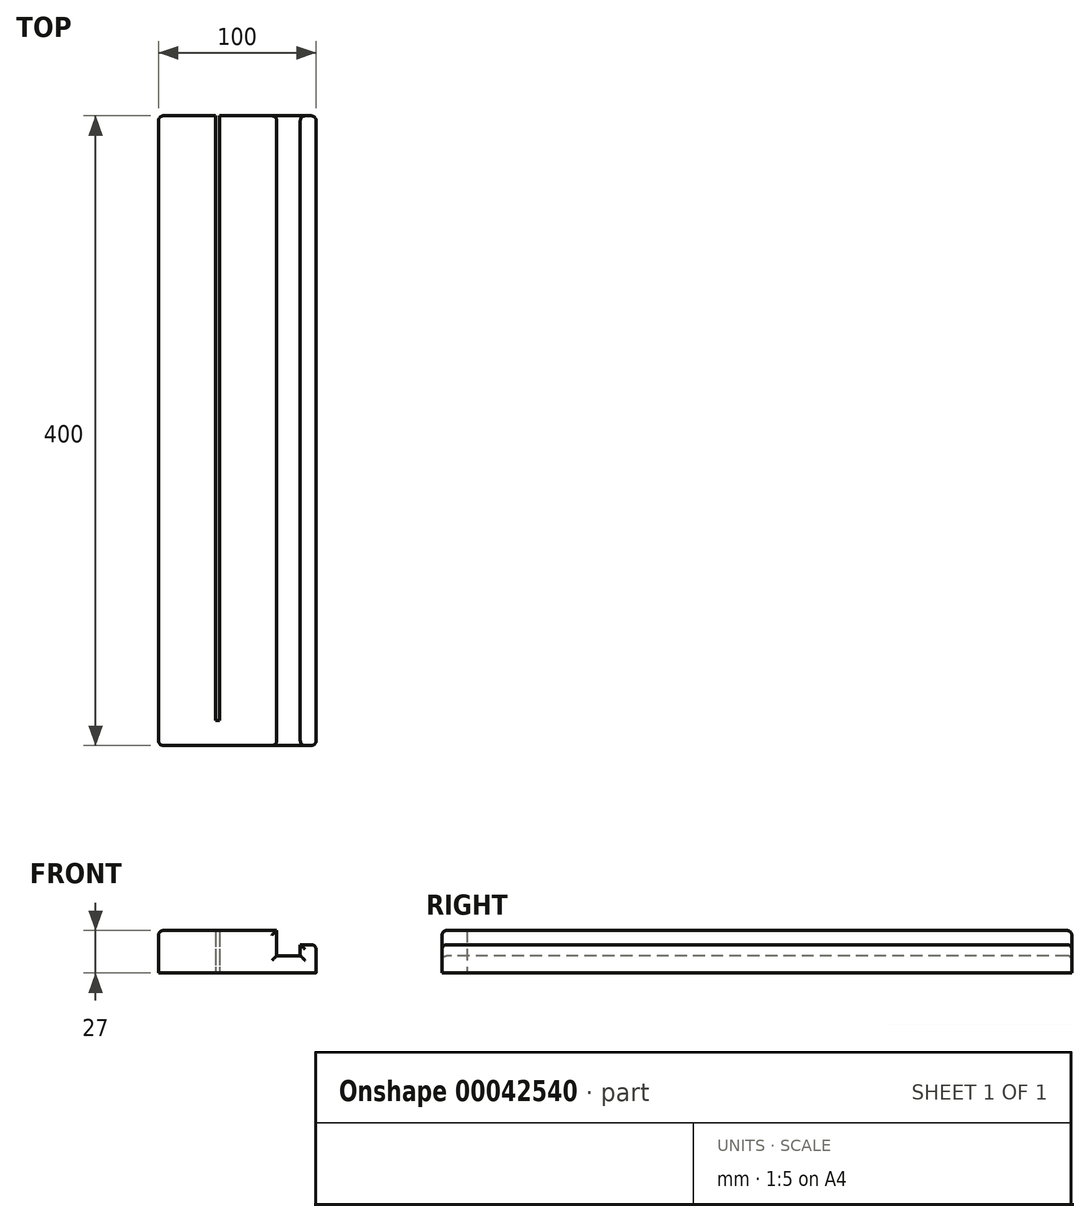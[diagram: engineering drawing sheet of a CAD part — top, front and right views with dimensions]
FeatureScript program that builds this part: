
annotation { "Feature Type Name" : "Feature", "Feature Type Description" : "" }
export const myFeature = defineFeature(function(context is Context, id is Id, definition is map)
    precondition{}
    {
        {
            assignVariable(context, id + "F0", {"name" : "WoodThickness", "anyValue" : 27});
        }
        {
            var Q0;
            Q0=qCreatedBy(makeId("Top.planeOp"),FACE);
            var sketch = newSketch(context, id + "F1", { "sketchPlane" : qUnion([Q0])});
            skLineSegment(sketch, "E0.bottom", {"start": v(-37.5, 200) * mm, "end": v(62.5, 200) * mm});
            skLineSegment(sketch, "E0.top", {"start": v(-37.5, -200) * mm, "end": v(62.5, -200) * mm});
            skLineSegment(sketch, "E0.left", {"start": v(-37.5, 200) * mm, "end": v(-37.5, -200) * mm});
            skLineSegment(sketch, "E0.right", {"start": v(62.5, 200) * mm, "end": v(62.5, -200) * mm});
            skCircle(sketch, "E1", {"center": v(0, -190) * mm, "radius": 6 * mm});
            skLineSegment(sketch, "E2.top", {"start": v(-1.25, 200) * mm, "end": v(1.25, 200) * mm});
            skLineSegment(sketch, "E2.left", {"start": v(-1.25, -184.13) * mm, "end": v(-1.25, 200) * mm});
            skLineSegment(sketch, "E2.right", {"start": v(1.25, -184.13) * mm, "end": v(1.25, 200) * mm});
            skLineSegment(sketch, "E3", {"start": v(52.5, 200) * mm, "end": v(52.5, -200) * mm});
            skLineSegment(sketch, "E4", {"start": v(37.5, 200) * mm, "end": v(37.5, -200) * mm});
            skSolve(sketch);
        }
        {
            var Q0;
            {var subQ6=sQuery(id+"F1.wireOp",EDGE,"E0.left");Q0=makeQuery(id+"F1.imprint","IMPRINT",FACE,{"disambiguationData":[TD([[makeQuery(id+"F1.imprint","IMPRINT",EDGE,{"derivedFrom":subQ6}),1.0]])]});}
            var Q1;
            Q1=makeQuery(id+"F1.imprint","IMPRINT",FACE,{"disambiguationData":[TD([[makeQuery(id+"F1.imprint","IMPRINT",EDGE,{"derivedFrom":sQuery(id+"F1.wireOp",EDGE,"E2.top")}),-1.0]])]});
            var Q2;
            {var subQ0=sQuery(id+"F1.wireOp",EDGE,"E1");var subQ2=makeQuery(id+"F1.imprint","INTERSECT",VERTEX,{"derivedFrom":[subQ0,sQuery(id+"F1.wireOp",EDGE,"E2.left")]});Q2=makeQuery(id+"F1.imprint","IMPRINT",FACE,{"disambiguationData":[TD([[makeQuery(id+"F1.imprint","IMPRINT",EDGE,{"disambiguationData":[TD([[subQ2,1.0]])],"derivedFrom":subQ0}),1.0]])]});}
            extrude(context, id + "F2", {"entities" : qUnion([Q0, Q1, Q2]), "depth" : (getVariable(context, 'WoodThickness')) * mm});
        }
        {
            var Q0;
            {var subQ1=sQuery(id+"F1.wireOp",EDGE,"E3");Q0=makeQuery(id+"F1.imprint","IMPRINT",FACE,{"disambiguationData":[TD([[makeQuery(id+"F1.imprint","IMPRINT",EDGE,{"derivedFrom":subQ1}),-1.0]])]});}
            extrude(context, id + "F3", {"entities" : qUnion([Q0]), "operationType" : NewBodyOperationType.ADD, "depth" : (getVariable(context, 'WoodThickness') - 16) * mm});
        }
        {
            var Q0;
            {var subQ1=sQuery(id+"F1.wireOp",EDGE,"E0.right");Q0=makeQuery(id+"F1.imprint","IMPRINT",FACE,{"disambiguationData":[TD([[makeQuery(id+"F1.imprint","IMPRINT",EDGE,{"derivedFrom":subQ1}),-1.0]])]});}
            extrude(context, id + "F4", {"entities" : qUnion([Q0]), "operationType" : NewBodyOperationType.ADD, "depth" : (getVariable(context, 'WoodThickness') - 9) * mm});
        }
        {
            var Q0;
            Q0=makeQuery(id+"F2.opExtrude","CAP_EDGE",EDGE,{"disambiguationData":[OSD([sQuery(id+"F1.wireOp",EDGE,"E0.left")])],"isStart":false});
            var Q1;
            Q1=makeQuery(id+"F2.opExtrude","CAP_EDGE",EDGE,{"disambiguationData":[OSD([sQuery(id+"F1.wireOp",EDGE,"E0.top")])],"isStart":false});
            var Q2;
            Q2=makeQuery(id+"F2.opExtrude","CAP_EDGE",EDGE,{"disambiguationData":[OSD([sQuery(id+"F1.wireOp",EDGE,"E0.bottom"),sQuery(id+"F1.wireOp",EDGE,"E2.top")])],"isStart":false});
            var Q3;
            Q3=makeQuery(id+"F4.opExtrude","CAP_EDGE",EDGE,{"disambiguationData":[OSD([sQuery(id+"F1.wireOp",EDGE,"E0.right")])],"isStart":false});
            var Q4;
            Q4=makeQuery(id+"F2.opExtrude","SWEPT_EDGE",EDGE,{"disambiguationData":[OSD([sQuery(id+"F1.wireOp",EDGE,"E0.top"),sQuery(id+"F1.wireOp",EDGE,"E4")])]});
            var Q5;
            Q5=makeQuery(id+"F2.opExtrude","SWEPT_EDGE",EDGE,{"disambiguationData":[OSD([sQuery(id+"F1.wireOp",EDGE,"E0.bottom"),sQuery(id+"F1.wireOp",EDGE,"E4")])]});
            var Q6;
            Q6=makeQuery(id+"F2.opExtrude","SWEPT_EDGE",EDGE,{"disambiguationData":[OSD([sQuery(id+"F1.wireOp",EDGE,"E0.top"),sQuery(id+"F1.wireOp",EDGE,"E0.left")])]});
            var Q7;
            Q7=makeQuery(id+"F4.opExtrude","SWEPT_EDGE",EDGE,{"disambiguationData":[OSD([sQuery(id+"F1.wireOp",EDGE,"E0.top"),sQuery(id+"F1.wireOp",EDGE,"E0.right")])]});
            var Q8;
            Q8=makeQuery(id+"F4.opExtrude","CAP_EDGE",EDGE,{"disambiguationData":[OSD([sQuery(id+"F1.wireOp",EDGE,"E0.top")])],"isStart":false});
            var Q9;
            Q9=makeQuery(id+"F4.opExtrude","SWEPT_EDGE",EDGE,{"disambiguationData":[OSD([sQuery(id+"F1.wireOp",EDGE,"E0.top"),sQuery(id+"F1.wireOp",EDGE,"E3")])]});
            var Q10;
            Q10=makeQuery(id+"F3.opExtrude","CAP_EDGE",EDGE,{"disambiguationData":[OSD([sQuery(id+"F1.wireOp",EDGE,"E0.top")])],"isStart":false});
            var Q11;
            Q11=makeQuery(id+"F3.opExtrude","CAP_EDGE",EDGE,{"disambiguationData":[OSD([sQuery(id+"F1.wireOp",EDGE,"E0.bottom")])],"isStart":false});
            var Q12;
            Q12=makeQuery(id+"F4.opExtrude","CAP_EDGE",EDGE,{"disambiguationData":[OSD([sQuery(id+"F1.wireOp",EDGE,"E0.bottom")])],"isStart":false});
            var Q13;
            Q13=makeQuery(id+"F4.opExtrude","SWEPT_EDGE",EDGE,{"disambiguationData":[OSD([sQuery(id+"F1.wireOp",EDGE,"E0.bottom"),sQuery(id+"F1.wireOp",EDGE,"E0.right")])]});
            var Q14;
            Q14=makeQuery(id+"F4.opExtrude","SWEPT_EDGE",EDGE,{"disambiguationData":[OSD([sQuery(id+"F1.wireOp",EDGE,"E0.bottom"),sQuery(id+"F1.wireOp",EDGE,"E3")])]});
            var Q15;
            Q15=makeQuery(id+"F2.opExtrude","SWEPT_EDGE",EDGE,{"disambiguationData":[OSD([sQuery(id+"F1.wireOp",EDGE,"E0.bottom"),sQuery(id+"F1.wireOp",EDGE,"E0.left")])]});
            fillet(context, id + "F5", {"entities" : qUnion([Q0, Q1, Q2, Q3, Q4, Q5, Q6, Q7, Q8, Q9, Q10, Q11, Q12, Q13, Q14, Q15]), "radius" : 3 * mm, "tangentPropagation" : true, "allowEdgeOverflow" : false});
        }
    });
